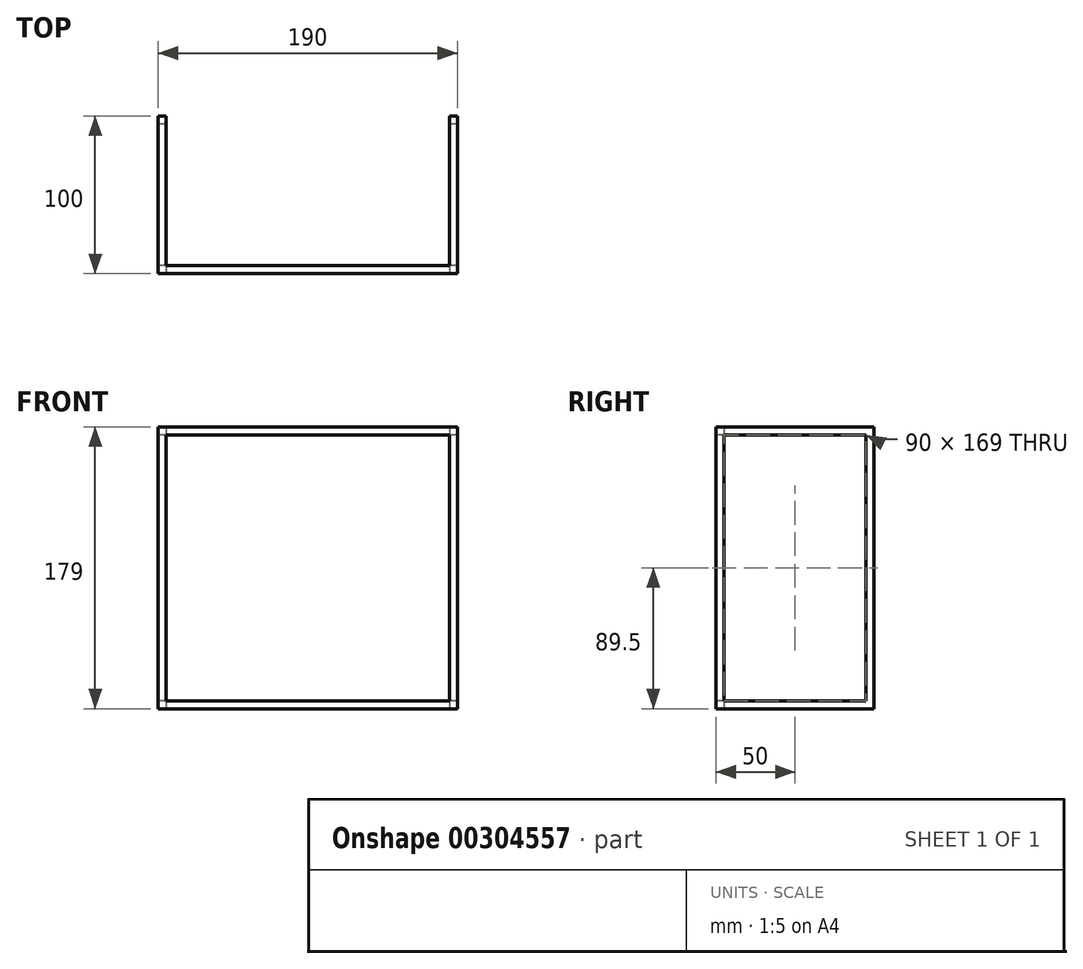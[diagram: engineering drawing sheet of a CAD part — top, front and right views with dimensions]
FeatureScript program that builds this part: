
annotation { "Feature Type Name" : "Feature", "Feature Type Description" : "" }
export const myFeature = defineFeature(function(context is Context, id is Id, definition is map)
    precondition{}
    {
        {
            var Q0;
            Q0=qCreatedBy(makeId("Top.planeOp"),FACE);
            var sketch = newSketch(context, id + "F0", { "sketchPlane" : qUnion([Q0])});
            skLineSegment(sketch, "E0", {"start": v(-74.2, 0) * mm, "end": v(115.8, 0) * mm});
            skLineSegment(sketch, "E1", {"start": v(-74.2, 0) * mm, "end": v(-74.2, 100) * mm});
            skLineSegment(sketch, "E2", {"start": v(115.8, 0) * mm, "end": v(115.8, 100) * mm});
            skLineSegment(sketch, "E3.0", {"start": v(-69.2, 5) * mm, "end": v(-69.2, 100) * mm});
            skLineSegment(sketch, "E3.1", {"start": v(-69.2, 5) * mm, "end": v(110.8, 5) * mm});
            skLineSegment(sketch, "E3.2", {"start": v(110.8, 5) * mm, "end": v(110.8, 100) * mm});
            skLineSegment(sketch, "E4", {"start": v(-74.2, 100) * mm, "end": v(-69.2, 100) * mm});
            skLineSegment(sketch, "E5", {"start": v(110.8, 100) * mm, "end": v(115.8, 100) * mm});
            skSolve(sketch);
        }
        {
            var Q0;
            Q0 = qSketchRegion(id + "F0", true);
            extrude(context, id + "F1", {"entities" : qUnion([Q0]), "depth" : 179 * mm});
        }
        {
            var Q0;
            Q0=makeQuery(id+"F1.opExtrude","SWEPT_FACE",FACE,{"disambiguationData":[OSD([sQuery(id+"F0.wireOp",EDGE,"E2")])]});
            var sketch = newSketch(context, id + "F2", { "sketchPlane" : qUnion([Q0])});
            skLineSegment(sketch, "E6.0", {"start": v(5, 5) * mm, "end": v(95, 5) * mm});
            skLineSegment(sketch, "E6.1", {"start": v(5, 174) * mm, "end": v(5, 5) * mm});
            skLineSegment(sketch, "E6.2", {"start": v(95, 174) * mm, "end": v(5, 174) * mm});
            skLineSegment(sketch, "E6.3", {"start": v(95, 5) * mm, "end": v(95, 174) * mm});
            skSolve(sketch);
        }
        {
            var Q0;
            Q0=makeQuery(id+"F2.imprint","IMPRINT",FACE,{"disambiguationData":[TD([[makeQuery(id+"F2.imprint","IMPRINT",EDGE,{"derivedFrom":sQuery(id+"F2.wireOp",EDGE,"E6.0")}),1.0]])]});
            extrude(context, id + "F3", {"entities" : qUnion([Q0]), "operationType" : NewBodyOperationType.REMOVE, "depth" : 200 * mm, "hasSecondDirection" : true, "secondDirectionOppositeDirection" : true, "secondDirectionDepth" : 200 * mm});
        }
        {
            var Q0;
            Q0=makeQuery(id+"F1.opExtrude","SWEPT_FACE",FACE,{"disambiguationData":[OSD([sQuery(id+"F0.wireOp",EDGE,"E0")])]});
            var sketch = newSketch(context, id + "F4", { "sketchPlane" : qUnion([Q0])});
            skLineSegment(sketch, "E7.0", {"start": v(-69.2, 5) * mm, "end": v(110.8, 5) * mm});
            skLineSegment(sketch, "E7.1", {"start": v(-69.2, 174) * mm, "end": v(-69.2, 5) * mm});
            skLineSegment(sketch, "E7.2", {"start": v(110.8, 174) * mm, "end": v(-69.2, 174) * mm});
            skLineSegment(sketch, "E7.3", {"start": v(110.8, 5) * mm, "end": v(110.8, 174) * mm});
            skSolve(sketch);
        }
        {
            var Q0;
            Q0=makeQuery(id+"F4.imprint","IMPRINT",FACE,{"disambiguationData":[TD([[makeQuery(id+"F4.imprint","IMPRINT",EDGE,{"derivedFrom":sQuery(id+"F4.wireOp",EDGE,"E7.0")}),1.0]])]});
            extrude(context, id + "F5", {"entities" : qUnion([Q0]), "operationType" : NewBodyOperationType.REMOVE, "oppositeDirection" : true, "depth" : 25 * mm});
        }
        {
            var Q0;
            Q0=makeQuery(id+"F1.opExtrude","SWEPT_FACE",FACE,{"disambiguationData":[OSD([sQuery(id+"F0.wireOp",EDGE,"E1")])]});
            var sketch = newSketch(context, id + "F6", { "sketchPlane" : qUnion([Q0])});
            skLineSegment(sketch, "E8.0", {"start": v(0, 176.5) * mm, "end": v(-100, 176.5) * mm, "construction": true});
            skLineSegment(sketch, "E9", {"start": v(-2.41, 0) * mm, "end": v(-2.41, 2.5) * mm, "construction": true});
            skLineSegment(sketch, "E10", {"start": v(-2.41, 2.5) * mm, "end": v(-2.41, 176.5) * mm});
            skSolve(sketch);
        }
        {
            var Q0;
            Q0=sQuery(id+"F6.wireOp",EDGE,"E10");
            extrude(context, id + "F7", {"bodyType" : ToolBodyType.SURFACE, "surfaceEntities" : qUnion([Q0]), "oppositeDirection" : true, "depth" : 189 * mm});
        }
        {
            var Q0;
            {var subQ1=makeQuery(id+"F3.opExtrude","SWEPT_FACE",FACE,{"disambiguationData":[OSD([sQuery(id+"F2.wireOp",EDGE,"E6.1")])]});var subQ2=makeQuery(id+"F1.opExtrude","SWEPT_FACE",FACE,{"disambiguationData":[OSD([sQuery(id+"F0.wireOp",EDGE,"E2")])]});var subQ3=makeQuery(id+"F1.opExtrude","SWEPT_FACE",FACE,{"disambiguationData":[OSD([sQuery(id+"F0.wireOp",EDGE,"E3.1")])]});Q0=makeQuery(id+"F5.boolean.opBoolean","SPLIT",FACE,{"disambiguationData":[TD([subQ2])],"derivedFrom":makeQuery(id+"F3.boolean.opBoolean","MERGE",FACE,{"derivedFrom":[subQ3,subQ1]})});}
            var sketch = newSketch(context, id + "F8", { "sketchPlane" : qUnion([Q0])});
            skLineSegment(sketch, "E11", {"start": v(-113.3, 174) * mm, "end": v(-113.3, 5) * mm});
            skSolve(sketch);
        }
        {
            var Q0;
            Q0=sQuery(id+"F8.wireOp",EDGE,"E11");
            extrude(context, id + "F9", {"bodyType" : ToolBodyType.SURFACE, "surfaceEntities" : qUnion([Q0]), "depth" : 89 * mm});
        }
        {
            var Q0;
            {var subQ0=makeQuery(id+"F3.opExtrude","SWEPT_FACE",FACE,{"disambiguationData":[OSD([sQuery(id+"F2.wireOp",EDGE,"E6.1")])]});var subQ1=makeQuery(id+"F1.opExtrude","SWEPT_FACE",FACE,{"disambiguationData":[OSD([sQuery(id+"F0.wireOp",EDGE,"E3.1")])]});var subQ3=makeQuery(id+"F1.opExtrude","SWEPT_FACE",FACE,{"disambiguationData":[OSD([sQuery(id+"F0.wireOp",EDGE,"E1")])]});Q0=makeQuery(id+"F5.boolean.opBoolean","SPLIT",FACE,{"disambiguationData":[TD([subQ3])],"derivedFrom":makeQuery(id+"F3.boolean.opBoolean","MERGE",FACE,{"derivedFrom":[subQ1,subQ0]})});}
            var sketch = newSketch(context, id + "F10", { "sketchPlane" : qUnion([Q0])});
            skLineSegment(sketch, "E12", {"start": v(71.7, 174) * mm, "end": v(71.7, 5) * mm});
            skSolve(sketch);
        }
        {
            var Q0;
            Q0=sQuery(id+"F10.wireOp",EDGE,"E12");
            extrude(context, id + "F11", {"bodyType" : ToolBodyType.SURFACE, "surfaceEntities" : qUnion([Q0]), "depth" : 89 * mm});
        }
    });
